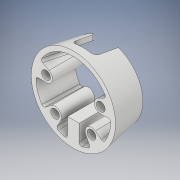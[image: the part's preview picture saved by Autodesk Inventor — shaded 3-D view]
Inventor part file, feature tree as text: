
AUTODESK INVENTOR PART (.ipt)
format: ipt  version: 2018 (Build 220112000, 112)  size: 446,976 bytes
history: native  units: in
note: dims shown in document units (in); Inventor stores cm internally (conversion verified against a paired STEP export)
features: extrude x9, sketch x6, projected_geometry x5, fillet x4, plane x2, shell x1, chamfer x1, split x1
ambient origin geometry x8: Origin, YZ Plane, XZ Plane, XY Plane, X Axis, Y Axis, Z Axis, Center Point
bodies: Solid1 (feature_tree)
feature tree (29):
  extrude  "Extrusion1"  Depth=0.3937in
  shell  "Shell1"  Thickness=0.3937in
  extrude  "Extrusion2"  Depth=0.3937in TaperAngle=0.0deg
  plane  "Work Plane1"
  extrude  "Extrusion3"  Depth=0.1969in
  fillet  "Fillet1"  Radius=0.1969in
  extrude  "Extrusion4"  TaperAngle=0.0deg  [1 undecoded]
  extrude  "Extrusion5"  Depth=0.0787in TaperAngle=0.0deg
  plane  "Work Plane2"
  sketch  "Sketch6"  dims[d13=0.5906in d14=0.0in d15=0.0in]
  extrude  "Extrusion6"  Depth=0.3937in
  extrude  "Extrusion7"  Depth=0.3937in
  extrude  "Extrusion8"  Depth=0.3937in
  extrude  "Extrusion9"  Depth=0.3937in
  fillet  "Fillet2"  Radius=0.2953in
  fillet  "Fillet3"  Radius=0.2953in
  chamfer  "Chamfer1"  Distance=0.2953in
  split  "Split1"
  fillet  "Fillet5"  Radius=0.9055in
  sketch  "Sketch2"  dims[d0=1.1811in d1=0.0687in d2=0.1575in d3=0.3937in]
  sketch  "Sketch4"  dims[d4=0.3937in d5=0.8661in d6=0.0in]
  sketch  "Sketch5"  dims[d7=-0.0669in d11=0.1969in d12=0.1969in]
  projected_geometry  "Projected Loop1"
  sketch  "Sketch7"  dims[d16=0.0787in d17=0.9055in d18=0.0in]
  sketch  "Sketch8"  dims[d19=0.1575in d20=0.1575in d21=0.1575in d22=0.1575in d23=0.2953in d24=0.2953in d25=0.2953in d26=0.2953in d27=0.9055in d28=0.0in d29=0.4331in d30=0.4331in d31=0.4331in d32=0.4331in d33=-0.1181in d34=0.0in d35=0.0in d36=0.9055in d37=0.0in d38=0.9055in d39=0.0in d40=0.9055in d41=0.0in d42=0.0787in d43=0.0394in d44=0.0787in d45=45.0deg d46=0.1575in d48=0.0787in d51=2.093in d53=0.3937in d54=0.9449in d55=0.1599in d56=0.1054in d57=0.1064in d58=0.3406in d59=0.3392in d60=0.952in d61=0.952in d62=0.9377in d63=0.9456in]
  projected_geometry  "Projected Loop2"
  projected_geometry  "Projected Loop3"
  projected_geometry  "Projected Loop4"
  projected_geometry  "Projected Loop5"
note: 1 required parameter value undecoded (feature->parameter linkage not recoverable at this tier; creation-order binding heuristic only, values carry confidence <= 0.55)
